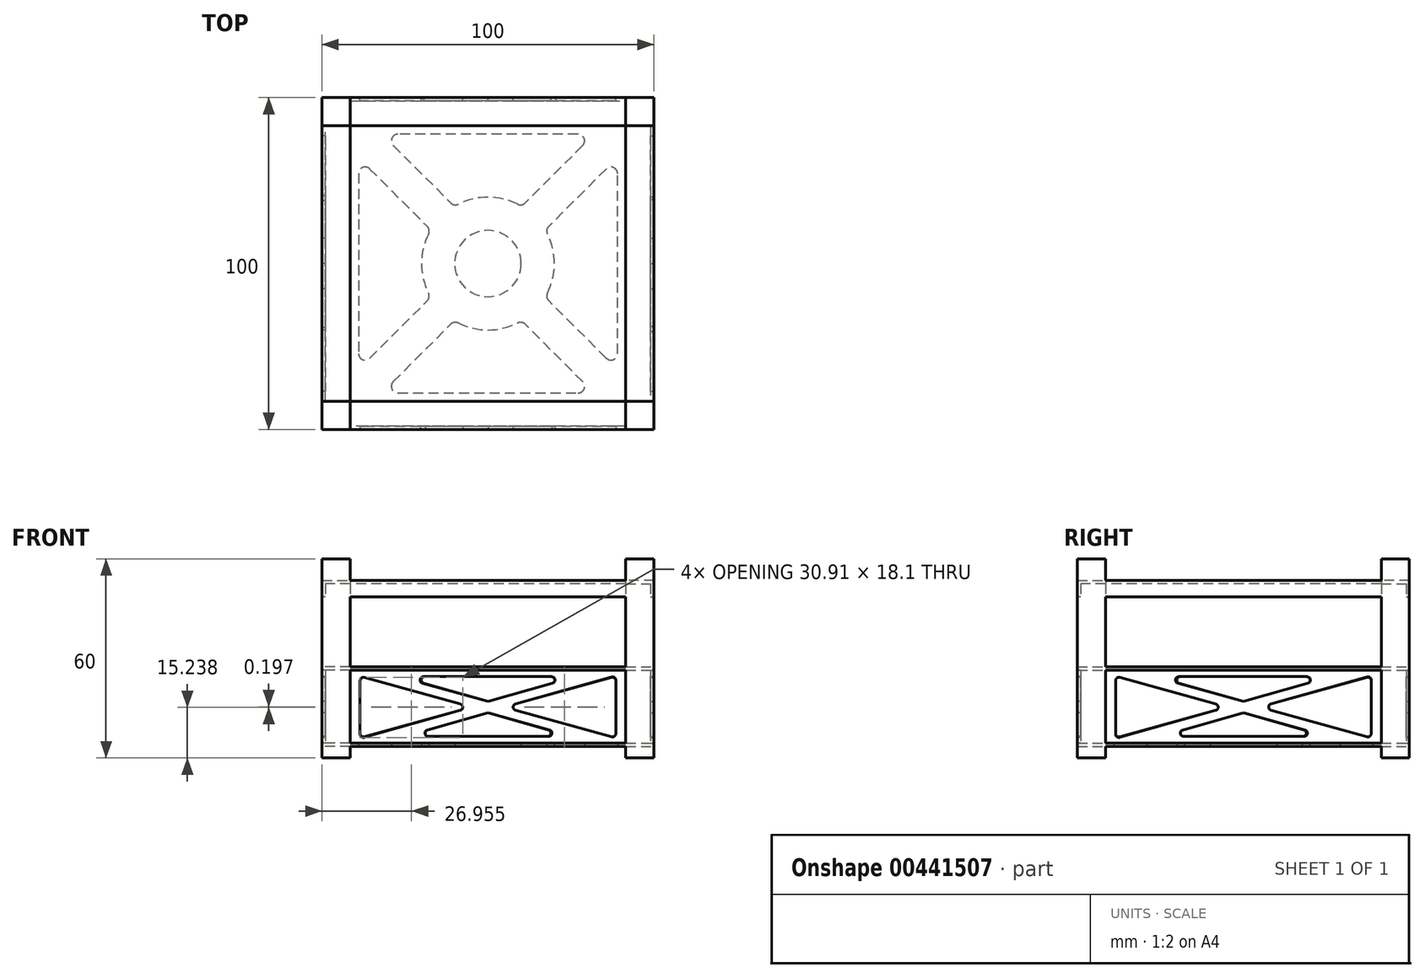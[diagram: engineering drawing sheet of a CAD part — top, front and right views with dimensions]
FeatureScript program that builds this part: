
annotation { "Feature Type Name" : "Feature", "Feature Type Description" : "" }
export const myFeature = defineFeature(function(context is Context, id is Id, definition is map)
    precondition{}
    {
        {
            var Q0;
            Q0=qCreatedBy(makeId("Top.planeOp"),FACE);
            var sketch = newSketch(context, id + "F0", { "sketchPlane" : qUnion([Q0])});
            skLineSegment(sketch, "E0.MirrorCS", {"start": v(-50, -50) * mm, "end": v(-41.5, -50) * mm});
            skLineSegment(sketch, "E1.MirrorCS", {"start": v(-50, -41.5) * mm, "end": v(-41.5, -41.5) * mm});
            skLineSegment(sketch, "E2.MirrorCS", {"start": v(-50, -50) * mm, "end": v(-50, -41.5) * mm});
            skLineSegment(sketch, "E3.MirrorCS", {"start": v(-41.5, -50) * mm, "end": v(-41.5, -41.5) * mm});
            skSolve(sketch);
        }
        {
            var Q0;
            Q0 = qSketchRegion(id + "F0", true);
            extrude(context, id + "F1", {"entities" : qUnion([Q0]), "depth" : 60 * mm});
        }
        {
            var Q0;
            Q0=makeQuery(id+"F1.opExtrude","SWEPT_FACE",FACE,{"disambiguationData":[OSD([sQuery(id+"F0.wireOp",EDGE,"E3.MirrorCS")])]});
            var sketch = newSketch(context, id + "F2", { "sketchPlane" : qUnion([Q0])});
            skLineSegment(sketch, "E4", {"start": v(-50, 48.5) * mm, "end": v(-50, 53.5) * mm});
            skLineSegment(sketch, "E5", {"start": v(-50, 53.5) * mm, "end": v(-41.5, 53.5) * mm});
            skLineSegment(sketch, "E6", {"start": v(-41.5, 53.5) * mm, "end": v(-41.5, 52.5) * mm});
            skLineSegment(sketch, "E7", {"start": v(-41.5, 52.5) * mm, "end": v(-49, 52.5) * mm});
            skLineSegment(sketch, "E8", {"start": v(-49, 52.5) * mm, "end": v(-49, 48.5) * mm});
            skLineSegment(sketch, "E9", {"start": v(-49, 48.5) * mm, "end": v(-50, 48.5) * mm});
            skSolve(sketch);
        }
        {
            var Q0;
            Q0 = qSketchRegion(id + "F2", true);
            extrude(context, id + "F3", {"entities" : qUnion([Q0]), "operationType" : NewBodyOperationType.ADD, "depth" : 83 * mm});
        }
        {
            var Q0;
            Q0=qCreatedBy(makeId("Front.planeOp"),FACE);
            var sketch = newSketch(context, id + "F4", { "sketchPlane" : qUnion([Q0])});
            skLineSegment(sketch, "E10", {"start": v(0, 70.01) * mm, "end": v(0, -54.88) * mm, "construction": true});
            skSolve(sketch);
        }
        {
            var Q0;
            Q0=makeQuery(id+"F1.opExtrude","SWEPT_BODY",BODY,{"disambiguationData":[OSD([sQuery(id+"F0.wireOp",EDGE,"E0.MirrorCS"),sQuery(id+"F0.wireOp",EDGE,"E1.MirrorCS"),sQuery(id+"F0.wireOp",EDGE,"E2.MirrorCS"),sQuery(id+"F0.wireOp",EDGE,"E3.MirrorCS")])]});
            var Q1;
            Q1=sQuery(id+"F4.wireOp",EDGE,"E10");
            circularPattern(context, id + "F5", {"entities" : qUnion([Q0]), "axis" : qUnion([Q1]), "angle" : 360 * degree, "instanceCount" : 4, "equalSpace" : true});
        }
        {
            var Q0;
            Q0=makeQuery(id+"F1.opExtrude","SWEPT_BODY",BODY,{"disambiguationData":[OSD([sQuery(id+"F0.wireOp",EDGE,"E0.MirrorCS"),sQuery(id+"F0.wireOp",EDGE,"E1.MirrorCS"),sQuery(id+"F0.wireOp",EDGE,"E2.MirrorCS"),sQuery(id+"F0.wireOp",EDGE,"E3.MirrorCS")])]});
            var Q1;
            Q1=makeQuery(id+"F5.opPattern","COPY",BODY,{"derivedFrom":makeQuery(id+"F1.opExtrude","SWEPT_BODY",BODY,{"disambiguationData":[OSD([sQuery(id+"F0.wireOp",EDGE,"E0.MirrorCS"),sQuery(id+"F0.wireOp",EDGE,"E1.MirrorCS"),sQuery(id+"F0.wireOp",EDGE,"E2.MirrorCS"),sQuery(id+"F0.wireOp",EDGE,"E3.MirrorCS")])]}),"instanceName":"1"});
            var Q2;
            Q2=makeQuery(id+"F5.opPattern","COPY",BODY,{"derivedFrom":makeQuery(id+"F1.opExtrude","SWEPT_BODY",BODY,{"disambiguationData":[OSD([sQuery(id+"F0.wireOp",EDGE,"E0.MirrorCS"),sQuery(id+"F0.wireOp",EDGE,"E1.MirrorCS"),sQuery(id+"F0.wireOp",EDGE,"E2.MirrorCS"),sQuery(id+"F0.wireOp",EDGE,"E3.MirrorCS")])]}),"instanceName":"2"});
            var Q3;
            Q3=makeQuery(id+"F5.opPattern","COPY",BODY,{"derivedFrom":makeQuery(id+"F1.opExtrude","SWEPT_BODY",BODY,{"disambiguationData":[OSD([sQuery(id+"F0.wireOp",EDGE,"E0.MirrorCS"),sQuery(id+"F0.wireOp",EDGE,"E1.MirrorCS"),sQuery(id+"F0.wireOp",EDGE,"E2.MirrorCS"),sQuery(id+"F0.wireOp",EDGE,"E3.MirrorCS")])]}),"instanceName":"3"});
            booleanBodies(context, id + "F6", {"operationType" : BooleanOperationType.UNION, "tools" : qUnion([Q0, Q1, Q2, Q3])});
        }
        {
            var Q0;
            Q0=qCreatedBy(makeId("Top.planeOp"),FACE);
            cPlane(context, id + "F7", {"entities" : qUnion([Q0]), "cplaneType" : CPlaneType.OFFSET, "offset" : 3.5 * mm, "width" : 150 * mm, "height" : 150 * mm});
        }
        {
            var Q0;
            Q0=qCreatedBy(id+"F7.planeOp",FACE);
            var sketch = newSketch(context, id + "F8", { "sketchPlane" : qUnion([Q0])});
            skLineSegment(sketch, "E11", {"start": v(-50, 41.5) * mm, "end": v(-41.5, 41.5) * mm});
            skLineSegment(sketch, "E12", {"start": v(-41.5, 41.5) * mm, "end": v(-41.5, 50) * mm});
            skLineSegment(sketch, "E13.1.0", {"start": v(41.5, 50) * mm, "end": v(41.5, 41.5) * mm});
            skLineSegment(sketch, "E13.1.1", {"start": v(41.5, 41.5) * mm, "end": v(50, 41.5) * mm});
            skLineSegment(sketch, "E13.2.0", {"start": v(50, -41.5) * mm, "end": v(41.5, -41.5) * mm});
            skLineSegment(sketch, "E13.2.1", {"start": v(41.5, -41.5) * mm, "end": v(41.5, -50) * mm});
            skLineSegment(sketch, "E13.3.0", {"start": v(-41.5, -50) * mm, "end": v(-41.5, -41.5) * mm});
            skLineSegment(sketch, "E13.3.1", {"start": v(-41.5, -41.5) * mm, "end": v(-50, -41.5) * mm});
            skPoint(sketch, "E13.center", {"position": v(0, 0) * mm});
            skLineSegment(sketch, "E13.anchor1", {"start": v(0, 0) * mm, "end": v(-50, 41.5) * mm, "construction": true});
            skLineSegment(sketch, "E13.anchor2", {"start": v(0, 0) * mm, "end": v(-41.5, -50) * mm, "construction": true});
            skLineSegment(sketch, "E14", {"start": v(-50, 41.5) * mm, "end": v(-50, -41.5) * mm});
            skLineSegment(sketch, "E15", {"start": v(-41.5, -50) * mm, "end": v(41.5, -50) * mm});
            skLineSegment(sketch, "E16", {"start": v(50, -41.5) * mm, "end": v(50, 41.5) * mm});
            skLineSegment(sketch, "E17", {"start": v(41.5, 50) * mm, "end": v(-41.5, 50) * mm});
            skCircle(sketch, "E18", {"center": v(0, 0) * mm, "radius": 10 * mm});
            skArc(sketch, "E19", {"start": v(-17.9, 8.9) * mm, "mid": v(-20, 0) * mm, "end": v(-17.9, -8.9) * mm});
            skLineSegment(sketch, "E20", {"start": v(-39, 27.1) * mm, "end": v(-39, -27.1) * mm});
            skLineSegment(sketch, "E21", {"start": v(-35.59, -28.51) * mm, "end": v(-18.28, -11.21) * mm});
            skLineSegment(sketch, "E22", {"start": v(-35.59, 28.51) * mm, "end": v(-18.28, 11.21) * mm});
            skLineSegment(sketch, "E23", {"start": v(41.5, 41.5) * mm, "end": v(-41.5, -41.5) * mm, "construction": true});
            skLineSegment(sketch, "E24.1.0", {"start": v(-27.1, -39) * mm, "end": v(27.1, -39) * mm});
            skLineSegment(sketch, "E24.1.1", {"start": v(-28.51, -35.59) * mm, "end": v(-11.21, -18.28) * mm});
            skLineSegment(sketch, "E24.1.2", {"start": v(28.51, -35.59) * mm, "end": v(11.21, -18.28) * mm});
            skLineSegment(sketch, "E24.2.0", {"start": v(39, -27.1) * mm, "end": v(39, 27.1) * mm});
            skLineSegment(sketch, "E24.2.1", {"start": v(35.59, -28.51) * mm, "end": v(18.28, -11.21) * mm});
            skLineSegment(sketch, "E24.2.2", {"start": v(35.59, 28.51) * mm, "end": v(18.28, 11.21) * mm});
            skLineSegment(sketch, "E24.3.0", {"start": v(27.1, 39) * mm, "end": v(-27.1, 39) * mm});
            skLineSegment(sketch, "E24.3.1", {"start": v(28.51, 35.59) * mm, "end": v(11.21, 18.28) * mm});
            skLineSegment(sketch, "E24.3.2", {"start": v(-28.51, 35.59) * mm, "end": v(-11.21, 18.28) * mm});
            skArc(sketch, "E25.trimOffspring", {"start": v(8.9, 17.9) * mm, "mid": v(0, 20) * mm, "end": v(-8.9, 17.9) * mm});
            skArc(sketch, "E26.trimOffspring", {"start": v(17.9, -8.9) * mm, "mid": v(20, 0) * mm, "end": v(17.9, 8.9) * mm});
            skArc(sketch, "E27.trimOffspring", {"start": v(-8.9, -17.9) * mm, "mid": v(0, -20) * mm, "end": v(8.9, -17.9) * mm});
            skPoint(sketch, "E28.visualSharp", {"position": v(-39, -31.93) * mm});
            skArc(sketch, "E28.filletArc", {"start": v(-39, -27.1) * mm, "mid": v(-37.77, -28.95) * mm, "end": v(-35.59, -28.51) * mm});
            skPoint(sketch, "E29.visualSharp", {"position": v(-17.23, -10.16) * mm});
            skArc(sketch, "E29.filletArc", {"start": v(-18.28, -11.21) * mm, "mid": v(-17.72, -10.12) * mm, "end": v(-17.9, -8.9) * mm});
            skPoint(sketch, "E30.visualSharp", {"position": v(-17.23, 10.16) * mm});
            skArc(sketch, "E30.filletArc", {"start": v(-17.9, 8.9) * mm, "mid": v(-17.72, 10.12) * mm, "end": v(-18.28, 11.21) * mm});
            skPoint(sketch, "E31.visualSharp", {"position": v(-39, 31.93) * mm});
            skArc(sketch, "E31.filletArc", {"start": v(-35.59, 28.51) * mm, "mid": v(-37.77, 28.95) * mm, "end": v(-39, 27.1) * mm});
            skPoint(sketch, "E32.visualSharp", {"position": v(-31.93, 39) * mm});
            skArc(sketch, "E32.filletArc", {"start": v(-27.1, 39) * mm, "mid": v(-28.95, 37.77) * mm, "end": v(-28.51, 35.59) * mm});
            skPoint(sketch, "E33.visualSharp", {"position": v(31.93, 39) * mm});
            skArc(sketch, "E33.filletArc", {"start": v(28.51, 35.59) * mm, "mid": v(28.95, 37.77) * mm, "end": v(27.1, 39) * mm});
            skPoint(sketch, "E34.visualSharp", {"position": v(10.16, 17.23) * mm});
            skArc(sketch, "E34.filletArc", {"start": v(8.9, 17.9) * mm, "mid": v(10.12, 17.72) * mm, "end": v(11.21, 18.28) * mm});
            skPoint(sketch, "E35.visualSharp", {"position": v(-10.16, 17.23) * mm});
            skArc(sketch, "E35.filletArc", {"start": v(-11.21, 18.28) * mm, "mid": v(-10.12, 17.72) * mm, "end": v(-8.9, 17.9) * mm});
            skPoint(sketch, "E36.visualSharp", {"position": v(39, 31.93) * mm});
            skArc(sketch, "E36.filletArc", {"start": v(39, 27.1) * mm, "mid": v(37.77, 28.95) * mm, "end": v(35.59, 28.51) * mm});
            skPoint(sketch, "E37.visualSharp", {"position": v(17.23, 10.16) * mm});
            skArc(sketch, "E37.filletArc", {"start": v(18.28, 11.21) * mm, "mid": v(17.72, 10.12) * mm, "end": v(17.9, 8.9) * mm});
            skPoint(sketch, "E38.visualSharp", {"position": v(17.23, -10.16) * mm});
            skArc(sketch, "E38.filletArc", {"start": v(17.9, -8.9) * mm, "mid": v(17.72, -10.12) * mm, "end": v(18.28, -11.21) * mm});
            skPoint(sketch, "E39.visualSharp", {"position": v(39, -31.93) * mm});
            skArc(sketch, "E39.filletArc", {"start": v(35.59, -28.51) * mm, "mid": v(37.77, -28.95) * mm, "end": v(39, -27.1) * mm});
            skPoint(sketch, "E40.visualSharp", {"position": v(31.93, -39) * mm});
            skArc(sketch, "E40.filletArc", {"start": v(27.1, -39) * mm, "mid": v(28.95, -37.77) * mm, "end": v(28.51, -35.59) * mm});
            skPoint(sketch, "E41.visualSharp", {"position": v(10.16, -17.23) * mm});
            skArc(sketch, "E41.filletArc", {"start": v(11.21, -18.28) * mm, "mid": v(10.12, -17.72) * mm, "end": v(8.9, -17.9) * mm});
            skPoint(sketch, "E42.visualSharp", {"position": v(-10.16, -17.23) * mm});
            skArc(sketch, "E42.filletArc", {"start": v(-8.9, -17.9) * mm, "mid": v(-10.12, -17.72) * mm, "end": v(-11.21, -18.28) * mm});
            skPoint(sketch, "E43.visualSharp", {"position": v(-31.93, -39) * mm});
            skArc(sketch, "E43.filletArc", {"start": v(-28.51, -35.59) * mm, "mid": v(-28.95, -37.77) * mm, "end": v(-27.1, -39) * mm});
            skSolve(sketch);
        }
        {
            var Q0;
            Q0 = qSketchRegion(id + "F8", true);
            extrude(context, id + "F9", {"entities" : qUnion([Q0]), "operationType" : NewBodyOperationType.ADD, "depth" : 1 * mm});
        }
        {
            var Q0;
            Q0=qCreatedBy(makeId("Top.planeOp"),FACE);
            cPlane(context, id + "F10", {"entities" : qUnion([Q0]), "cplaneType" : CPlaneType.OFFSET, "offset" : 26.5 * mm, "width" : 150 * mm, "height" : 150 * mm});
        }
        {
            var Q0;
            Q0=qCreatedBy(id+"F10.planeOp",FACE);
            var sketch = newSketch(context, id + "F11", { "sketchPlane" : qUnion([Q0])});
            skLineSegment(sketch, "E44", {"start": v(-50, 41.5) * mm, "end": v(-41.5, 41.5) * mm});
            skLineSegment(sketch, "E45", {"start": v(-41.5, 41.5) * mm, "end": v(-41.5, 50) * mm});
            skLineSegment(sketch, "E46", {"start": v(-41.5, 50) * mm, "end": v(41.5, 50) * mm});
            skLineSegment(sketch, "E47", {"start": v(41.5, 50) * mm, "end": v(41.5, 41.5) * mm});
            skLineSegment(sketch, "E48", {"start": v(41.5, 41.5) * mm, "end": v(50, 41.5) * mm});
            skLineSegment(sketch, "E49", {"start": v(50, 41.5) * mm, "end": v(50, -41.5) * mm});
            skLineSegment(sketch, "E50", {"start": v(50, -41.5) * mm, "end": v(41.5, -41.5) * mm});
            skLineSegment(sketch, "E51", {"start": v(41.5, -41.5) * mm, "end": v(41.5, -50) * mm});
            skLineSegment(sketch, "E52", {"start": v(41.5, -50) * mm, "end": v(-41.5, -50) * mm});
            skLineSegment(sketch, "E53", {"start": v(-41.5, -50) * mm, "end": v(-41.5, -41.5) * mm});
            skLineSegment(sketch, "E54", {"start": v(-41.5, -41.5) * mm, "end": v(-50, -41.5) * mm});
            skLineSegment(sketch, "E55", {"start": v(-50, -41.5) * mm, "end": v(-50, 41.5) * mm});
            skSolve(sketch);
        }
        {
            var Q0;
            Q0 = qSketchRegion(id + "F11", true);
            extrude(context, id + "F12", {"entities" : qUnion([Q0]), "operationType" : NewBodyOperationType.ADD, "depth" : 1 * mm});
        }
        {
            var Q0;
            Q0=makeQuery(id+"F12.boolean.opBoolean","MERGE",FACE,{"derivedFrom":[makeQuery(id+"F9.boolean.opBoolean","MERGE",FACE,{"derivedFrom":[makeQuery(id+"F6.opBoolean","MERGE",FACE,{"derivedFrom":[makeQuery(id+"F3.boolean.opBoolean","MERGE",FACE,{"derivedFrom":[makeQuery(id+"F1.opExtrude","SWEPT_FACE",FACE,{"disambiguationData":[OSD([sQuery(id+"F0.wireOp",EDGE,"E0.MirrorCS")])]}),makeQuery(id+"F3.opExtrude","SWEPT_FACE",FACE,{"disambiguationData":[OSD([sQuery(id+"F2.wireOp",EDGE,"E4")])]})]}),makeQuery(id+"F5.opPattern","COPY",FACE,{"derivedFrom":makeQuery(id+"F1.opExtrude","SWEPT_FACE",FACE,{"disambiguationData":[OSD([sQuery(id+"F0.wireOp",EDGE,"E2.MirrorCS")])]}),"instanceName":"3"})]}),makeQuery(id+"F9.opExtrude","SWEPT_FACE",FACE,{"disambiguationData":[OSD([sQuery(id+"F8.wireOp",EDGE,"E15")])]})]}),makeQuery(id+"F12.opExtrude","SWEPT_FACE",FACE,{"disambiguationData":[OSD([sQuery(id+"F11.wireOp",EDGE,"E52")])]})]});
            var sketch = newSketch(context, id + "F13", { "sketchPlane" : qUnion([Q0])});
            skLineSegment(sketch, "E56", {"start": v(-41.5, 26.5) * mm, "end": v(-41.5, 4.5) * mm});
            skLineSegment(sketch, "E57", {"start": v(-41.5, 4.5) * mm, "end": v(41.5, 4.5) * mm});
            skLineSegment(sketch, "E58", {"start": v(41.5, 4.5) * mm, "end": v(41.5, 26.5) * mm});
            skLineSegment(sketch, "E59", {"start": v(41.5, 26.5) * mm, "end": v(-41.5, 26.5) * mm});
            skLineSegment(sketch, "E60", {"start": v(-38.5, 23.29) * mm, "end": v(-38.5, 7.19) * mm});
            skLineSegment(sketch, "E61", {"start": v(-37.23, 6.23) * mm, "end": v(-8.32, 14.35) * mm});
            skLineSegment(sketch, "E62", {"start": v(-8.32, 16.28) * mm, "end": v(-37.23, 24.25) * mm});
            skLineSegment(sketch, "E63", {"start": v(-19.46, 24.5) * mm, "end": v(19.08, 24.5) * mm});
            skLineSegment(sketch, "E64", {"start": v(19.35, 22.54) * mm, "end": v(0, 17.1) * mm});
            skLineSegment(sketch, "E65", {"start": v(0, 17.1) * mm, "end": v(-19.73, 22.54) * mm});
            skLineSegment(sketch, "E66", {"start": v(0, 13.58) * mm, "end": v(-18.19, 8.46) * mm});
            skLineSegment(sketch, "E67", {"start": v(-17.92, 6.5) * mm, "end": v(18.27, 6.5) * mm});
            skLineSegment(sketch, "E68", {"start": v(18.54, 8.46) * mm, "end": v(0, 13.58) * mm});
            skLineSegment(sketch, "E69", {"start": v(37.23, 24.45) * mm, "end": v(8.32, 16.32) * mm});
            skLineSegment(sketch, "E70", {"start": v(8.32, 14.4) * mm, "end": v(37.23, 6.42) * mm});
            skLineSegment(sketch, "E71", {"start": v(38.5, 7.39) * mm, "end": v(38.5, 23.48) * mm});
            skPoint(sketch, "E72.visualSharp", {"position": v(-4.86, 15.33) * mm});
            skArc(sketch, "E72.filletArc", {"start": v(-8.32, 14.35) * mm, "mid": v(-7.59, 15.32) * mm, "end": v(-8.32, 16.28) * mm});
            skPoint(sketch, "E73.visualSharp", {"position": v(-38.5, 5.87) * mm});
            skArc(sketch, "E73.filletArc", {"start": v(-38.5, 7.19) * mm, "mid": v(-38.1, 6.4) * mm, "end": v(-37.23, 6.23) * mm});
            skPoint(sketch, "E74.visualSharp", {"position": v(-25.17, 6.5) * mm});
            skArc(sketch, "E74.filletArc", {"start": v(-18.19, 8.46) * mm, "mid": v(-18.9, 7.36) * mm, "end": v(-17.92, 6.5) * mm});
            skPoint(sketch, "E75.visualSharp", {"position": v(25.66, 6.5) * mm});
            skArc(sketch, "E75.filletArc", {"start": v(18.27, 6.5) * mm, "mid": v(19.27, 7.37) * mm, "end": v(18.54, 8.46) * mm});
            skPoint(sketch, "E76.visualSharp", {"position": v(-38.5, 24.6) * mm});
            skArc(sketch, "E76.filletArc", {"start": v(-37.23, 24.25) * mm, "mid": v(-38.1, 24.08) * mm, "end": v(-38.5, 23.29) * mm});
            skPoint(sketch, "E77.visualSharp", {"position": v(-26.85, 24.5) * mm});
            skArc(sketch, "E77.filletArc", {"start": v(-19.46, 24.5) * mm, "mid": v(-20.45, 23.63) * mm, "end": v(-19.73, 22.54) * mm});
            skPoint(sketch, "E78.visualSharp", {"position": v(26.33, 24.5) * mm});
            skArc(sketch, "E78.filletArc", {"start": v(19.35, 22.54) * mm, "mid": v(20.07, 23.64) * mm, "end": v(19.08, 24.5) * mm});
            skPoint(sketch, "E79.visualSharp", {"position": v(4.86, 15.35) * mm});
            skArc(sketch, "E79.filletArc", {"start": v(8.32, 16.32) * mm, "mid": v(7.59, 15.35) * mm, "end": v(8.32, 14.4) * mm});
            skPoint(sketch, "E80.visualSharp", {"position": v(38.5, 6.07) * mm});
            skArc(sketch, "E80.filletArc", {"start": v(37.23, 6.42) * mm, "mid": v(38.1, 6.6) * mm, "end": v(38.5, 7.39) * mm});
            skPoint(sketch, "E81.visualSharp", {"position": v(38.5, 24.8) * mm});
            skArc(sketch, "E81.filletArc", {"start": v(38.5, 23.48) * mm, "mid": v(38.1, 24.28) * mm, "end": v(37.23, 24.45) * mm});
            skSolve(sketch);
        }
        {
            var Q0;
            Q0 = qSketchRegion(id + "F13", true);
            extrude(context, id + "F14", {"entities" : qUnion([Q0]), "oppositeDirection" : true, "depth" : 1 * mm});
        }
        {
            var Q0;
            Q0=makeQuery(id+"F14.opExtrude","SWEPT_BODY",BODY,{"disambiguationData":[OSD([sQuery(id+"F13.wireOp",EDGE,"E56"),sQuery(id+"F13.wireOp",EDGE,"E57"),sQuery(id+"F13.wireOp",EDGE,"E58"),sQuery(id+"F13.wireOp",EDGE,"E59"),sQuery(id+"F13.wireOp",EDGE,"E60"),sQuery(id+"F13.wireOp",EDGE,"E61"),sQuery(id+"F13.wireOp",EDGE,"E62"),sQuery(id+"F13.wireOp",EDGE,"E63"),sQuery(id+"F13.wireOp",EDGE,"E64"),sQuery(id+"F13.wireOp",EDGE,"E65"),sQuery(id+"F13.wireOp",EDGE,"E66"),sQuery(id+"F13.wireOp",EDGE,"E67"),sQuery(id+"F13.wireOp",EDGE,"E68"),sQuery(id+"F13.wireOp",EDGE,"E69"),sQuery(id+"F13.wireOp",EDGE,"E70"),sQuery(id+"F13.wireOp",EDGE,"E71"),sQuery(id+"F13.wireOp",EDGE,"E72.filletArc"),sQuery(id+"F13.wireOp",EDGE,"E73.filletArc"),sQuery(id+"F13.wireOp",EDGE,"E74.filletArc"),sQuery(id+"F13.wireOp",EDGE,"E75.filletArc"),sQuery(id+"F13.wireOp",EDGE,"E76.filletArc"),sQuery(id+"F13.wireOp",EDGE,"E77.filletArc"),sQuery(id+"F13.wireOp",EDGE,"E78.filletArc"),sQuery(id+"F13.wireOp",EDGE,"E79.filletArc"),sQuery(id+"F13.wireOp",EDGE,"E80.filletArc"),sQuery(id+"F13.wireOp",EDGE,"E81.filletArc")])]});
            var Q1;
            Q1=sQuery(id+"F4.wireOp",EDGE,"E10");
            circularPattern(context, id + "F15", {"entities" : qUnion([Q0]), "axis" : qUnion([Q1]), "angle" : 360 * degree, "instanceCount" : 4, "equalSpace" : true});
        }
    });
